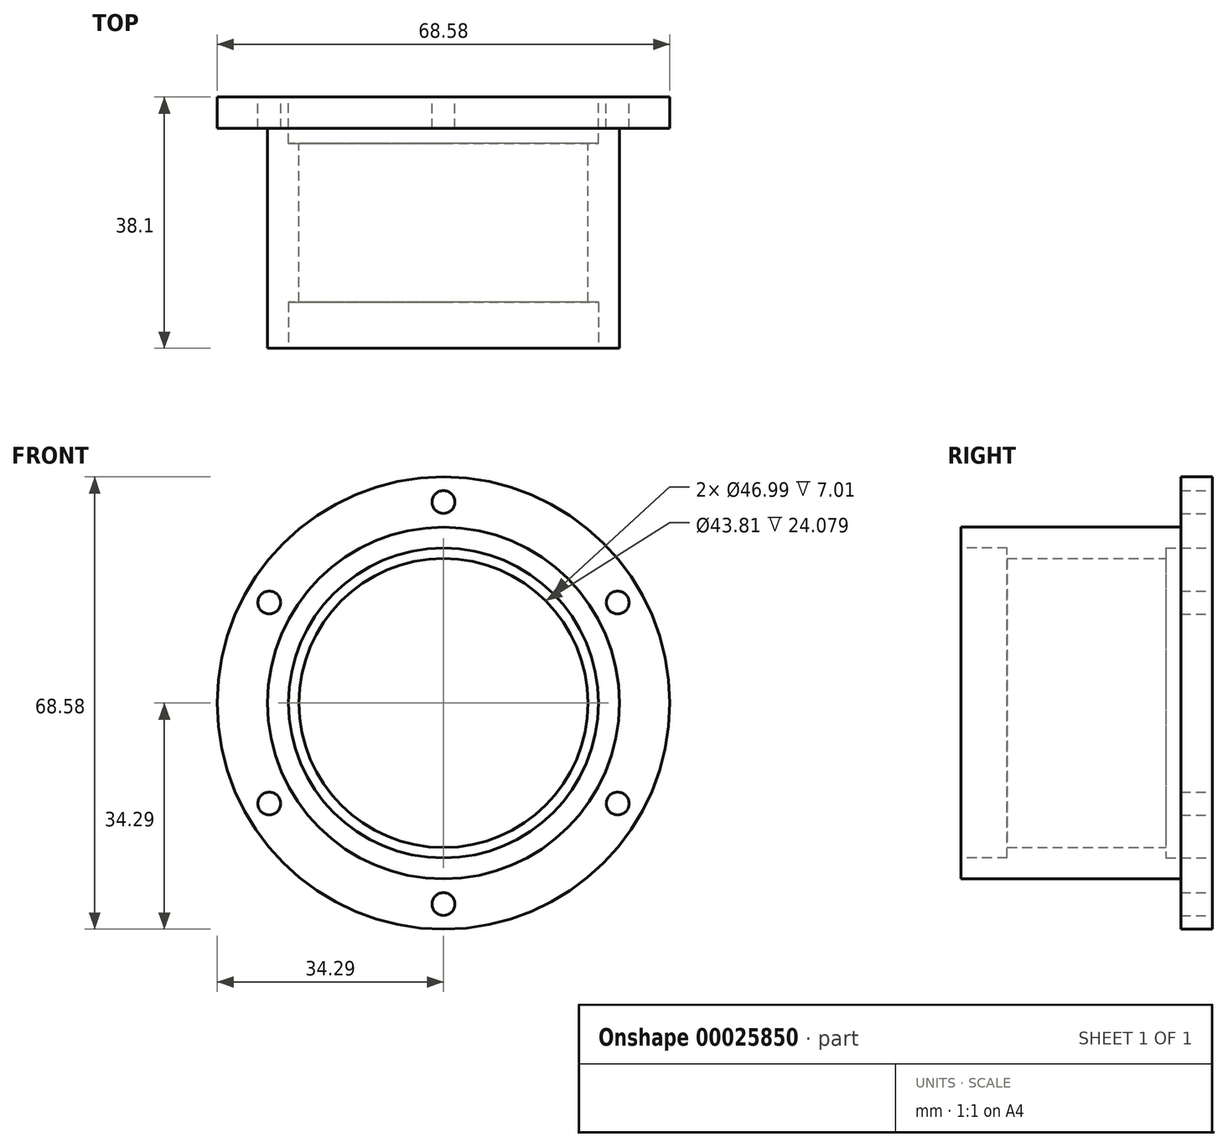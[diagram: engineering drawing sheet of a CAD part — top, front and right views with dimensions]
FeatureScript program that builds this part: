
annotation { "Feature Type Name" : "Feature", "Feature Type Description" : "" }
export const myFeature = defineFeature(function(context is Context, id is Id, definition is map)
    precondition{}
    {
        {
            var Q0;
            Q0=qCreatedBy(makeId("Front.planeOp"),FACE);
            var sketch = newSketch(context, id + "F0", { "sketchPlane" : qUnion([Q0])});
            skCircle(sketch, "E0", {"center": v(0, 0) * mm, "radius": 34.3 * mm});
            skCircle(sketch, "E1", {"center": v(0, 0) * mm, "radius": 30.48 * mm, "construction": true});
            skLineSegment(sketch, "E2.0", {"start": v(0, -30.48) * mm, "end": v(-26.4, -15.24) * mm, "construction": true});
            skLineSegment(sketch, "E2.1", {"start": v(-26.4, -15.24) * mm, "end": v(-26.4, 15.24) * mm, "construction": true});
            skLineSegment(sketch, "E2.2", {"start": v(-26.4, 15.24) * mm, "end": v(0, 30.48) * mm, "construction": true});
            skLineSegment(sketch, "E2.3", {"start": v(0, 30.48) * mm, "end": v(26.4, 15.24) * mm, "construction": true});
            skLineSegment(sketch, "E2.4", {"start": v(26.4, 15.24) * mm, "end": v(26.4, -15.24) * mm, "construction": true});
            skLineSegment(sketch, "E2.5", {"start": v(26.4, -15.24) * mm, "end": v(0, -30.48) * mm, "construction": true});
            skCircle(sketch, "E3", {"center": v(0, 30.48) * mm, "radius": 1.73 * mm});
            skCircle(sketch, "E4", {"center": v(-26.4, 15.24) * mm, "radius": 1.73 * mm});
            skCircle(sketch, "E5", {"center": v(-26.4, -15.24) * mm, "radius": 1.73 * mm});
            skCircle(sketch, "E6", {"center": v(0, -30.48) * mm, "radius": 1.73 * mm});
            skCircle(sketch, "E7", {"center": v(26.4, -15.24) * mm, "radius": 1.73 * mm});
            skCircle(sketch, "E8", {"center": v(26.4, 15.24) * mm, "radius": 1.73 * mm});
            skSolve(sketch);
        }
        {
            var Q0;
            Q0=makeQuery(id+"F0.imprint","IMPRINT",FACE,{"disambiguationData":[TD([[makeQuery(id+"F0.imprint","IMPRINT",EDGE,{"derivedFrom":sQuery(id+"F0.wireOp",EDGE,"E0")}),1.0]])]});
            extrude(context, id + "F1", {"entities" : qUnion([Q0]), "depth" : 4.78 * mm});
        }
        {
            var Q0;
            Q0=makeQuery(id+"F1.opExtrude","CAP_FACE",FACE,{"disambiguationData":[OSD([sQuery(id+"F0.wireOp",EDGE,"E0"),sQuery(id+"F0.wireOp",EDGE,"E3"),sQuery(id+"F0.wireOp",EDGE,"E4"),sQuery(id+"F0.wireOp",EDGE,"E5"),sQuery(id+"F0.wireOp",EDGE,"E6"),sQuery(id+"F0.wireOp",EDGE,"E7"),sQuery(id+"F0.wireOp",EDGE,"E8")])],"isStart":false});
            var sketch = newSketch(context, id + "F2", { "sketchPlane" : qUnion([Q0])});
            skCircle(sketch, "E9", {"center": v(0, 0) * mm, "radius": 26.67 * mm});
            skSolve(sketch);
        }
        {
            var Q0;
            Q0=makeQuery(id+"F2.imprint","IMPRINT",FACE,{"disambiguationData":[TD([[makeQuery(id+"F2.imprint","IMPRINT",EDGE,{"derivedFrom":sQuery(id+"F2.wireOp",EDGE,"E9")}),1.0]])]});
            extrude(context, id + "F3", {"entities" : qUnion([Q0]), "operationType" : NewBodyOperationType.ADD, "depth" : 33.32 * mm});
        }
        {
            var Q0;
            Q0=makeQuery(id+"F1.opExtrude","CAP_FACE",FACE,{"disambiguationData":[OSD([sQuery(id+"F0.wireOp",EDGE,"E0"),sQuery(id+"F0.wireOp",EDGE,"E3"),sQuery(id+"F0.wireOp",EDGE,"E4"),sQuery(id+"F0.wireOp",EDGE,"E5"),sQuery(id+"F0.wireOp",EDGE,"E6"),sQuery(id+"F0.wireOp",EDGE,"E7"),sQuery(id+"F0.wireOp",EDGE,"E8")])],"isStart":true});
            var sketch = newSketch(context, id + "F4", { "sketchPlane" : qUnion([Q0])});
            skCircle(sketch, "E10", {"center": v(0, 0) * mm, "radius": 23.5 * mm});
            skSolve(sketch);
        }
        {
            var Q0;
            Q0=makeQuery(id+"F4.imprint","IMPRINT",FACE,{"disambiguationData":[TD([[makeQuery(id+"F4.imprint","IMPRINT",EDGE,{"derivedFrom":sQuery(id+"F4.wireOp",EDGE,"E10")}),1.0]])]});
            extrude(context, id + "F5", {"entities" : qUnion([Q0]), "operationType" : NewBodyOperationType.REMOVE, "oppositeDirection" : true, "depth" : 7 * mm});
        }
        {
            var Q0;
            Q0=makeQuery(id+"F5.boolean.opBoolean","COPY",FACE,{"derivedFrom":makeQuery(id+"F5.opExtrude","CAP_FACE",FACE,{"disambiguationData":[OSD([sQuery(id+"F4.wireOp",EDGE,"E10")])],"isStart":false})});
            var sketch = newSketch(context, id + "F6", { "sketchPlane" : qUnion([Q0])});
            skCircle(sketch, "E11", {"center": v(0, 0) * mm, "radius": 21.9 * mm});
            skSolve(sketch);
        }
        {
            var Q0;
            Q0=makeQuery(id+"F6.imprint","IMPRINT",FACE,{"disambiguationData":[TD([[makeQuery(id+"F6.imprint","IMPRINT",EDGE,{"derivedFrom":sQuery(id+"F6.wireOp",EDGE,"E11")}),1.0]])]});
            extrude(context, id + "F7", {"entities" : qUnion([Q0]), "operationType" : NewBodyOperationType.REMOVE, "oppositeDirection" : true, "depth" : 24.08 * mm});
        }
        {
            var Q0;
            Q0=makeQuery(id+"F3.opExtrude","CAP_FACE",FACE,{"disambiguationData":[OSD([sQuery(id+"F2.wireOp",EDGE,"E9")])],"isStart":false});
            var sketch = newSketch(context, id + "F8", { "sketchPlane" : qUnion([Q0])});
            skCircle(sketch, "E12", {"center": v(0, 0) * mm, "radius": 23.5 * mm});
            skSolve(sketch);
        }
        {
            var Q0;
            Q0=makeQuery(id+"F8.imprint","IMPRINT",FACE,{"disambiguationData":[TD([[makeQuery(id+"F8.imprint","IMPRINT",EDGE,{"derivedFrom":sQuery(id+"F8.wireOp",EDGE,"E12")}),1.0]])]});
            extrude(context, id + "F9", {"entities" : qUnion([Q0]), "operationType" : NewBodyOperationType.REMOVE, "oppositeDirection" : true, "depth" : 7 * mm});
        }
    });
